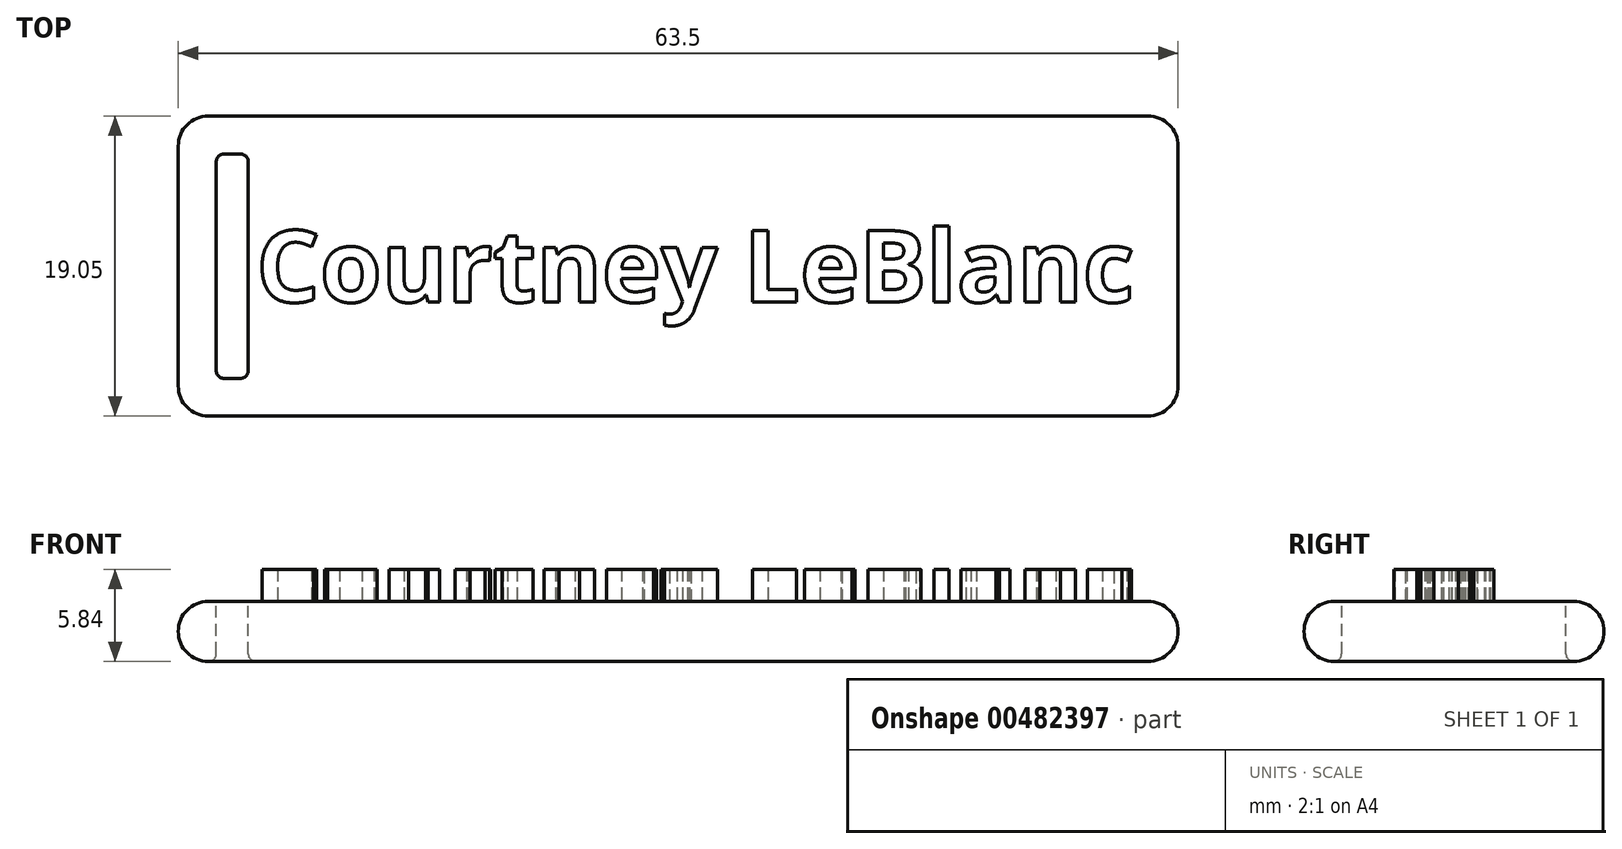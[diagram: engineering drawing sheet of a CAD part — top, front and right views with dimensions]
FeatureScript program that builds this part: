
annotation { "Feature Type Name" : "Feature", "Feature Type Description" : "" }
export const myFeature = defineFeature(function(context is Context, id is Id, definition is map)
    precondition{}
    {
        {
            var Q0;
            Q0=qCreatedBy(makeId("Top.planeOp"),FACE);
            var sketch = newSketch(context, id + "F0", { "sketchPlane" : qUnion([Q0])});
            skLineSegment(sketch, "E0.bottom", {"start": v(0, 0) * mm, "end": v(63.5, 0) * mm});
            skLineSegment(sketch, "E0.top", {"start": v(0, 19.05) * mm, "end": v(63.5, 19.05) * mm});
            skLineSegment(sketch, "E0.left", {"start": v(0, 0) * mm, "end": v(0, 19.05) * mm});
            skLineSegment(sketch, "E0.right", {"start": v(63.5, 0) * mm, "end": v(63.5, 19.05) * mm});
            skSolve(sketch);
        }
        {
            var Q0;
            Q0=makeQuery(id+"F0.imprint","IMPRINT",FACE,{"disambiguationData":[TD([[makeQuery(id+"F0.imprint","IMPRINT",EDGE,{"derivedFrom":sQuery(id+"F0.wireOp",EDGE,"E0.bottom")}),1.0]])]});
            extrude(context, id + "F1", {"entities" : qUnion([Q0]), "depth" : 3.8 * mm});
        }
        {
            var Q0;
            Q0=makeQuery(id+"F1.opExtrude","CAP_FACE",FACE,{"disambiguationData":[OSD([sQuery(id+"F0.wireOp",EDGE,"E0.bottom"),sQuery(id+"F0.wireOp",EDGE,"E0.top"),sQuery(id+"F0.wireOp",EDGE,"E0.left"),sQuery(id+"F0.wireOp",EDGE,"E0.right")])],"isStart":false});
            var sketch = newSketch(context, id + "F2", { "sketchPlane" : qUnion([Q0])});
            skText(sketch, "E1", { "text": "Courtney LeBlanc", "fontName": "OpenSans-Bold.ttf"});
            const initialGuessF2  = {"E1": [0.00495, 0.00724, 1, 0, 0.00457]};
            skSetInitialGuess(sketch, initialGuessF2);
            skSolve(sketch);
        }
        {
            var Q0;
            Q0 = qSketchRegion(id + "F2", true);
            extrude(context, id + "F3", {"entities" : qUnion([Q0]), "operationType" : NewBodyOperationType.ADD, "depth" : 2.03 * mm});
        }
        {
            var Q0;
            Q0=makeQuery(id+"F1.opExtrude","SWEPT_EDGE",EDGE,{"disambiguationData":[OSD([sQuery(id+"F0.wireOp",EDGE,"E0.top"),sQuery(id+"F0.wireOp",EDGE,"E0.right")])]});
            var Q1;
            Q1=makeQuery(id+"F1.opExtrude","CAP_EDGE",EDGE,{"disambiguationData":[OSD([sQuery(id+"F0.wireOp",EDGE,"E0.right")])],"isStart":false});
            var Q2;
            Q2=makeQuery(id+"F1.opExtrude","CAP_EDGE",EDGE,{"disambiguationData":[OSD([sQuery(id+"F0.wireOp",EDGE,"E0.top")])],"isStart":false});
            var Q3;
            Q3=makeQuery(id+"F1.opExtrude","CAP_EDGE",EDGE,{"disambiguationData":[OSD([sQuery(id+"F0.wireOp",EDGE,"E0.top")])],"isStart":true});
            var Q4;
            Q4=makeQuery(id+"F1.opExtrude","CAP_EDGE",EDGE,{"disambiguationData":[OSD([sQuery(id+"F0.wireOp",EDGE,"E0.right")])],"isStart":true});
            var Q5;
            Q5=makeQuery(id+"F1.opExtrude","SWEPT_EDGE",EDGE,{"disambiguationData":[OSD([sQuery(id+"F0.wireOp",EDGE,"E0.bottom"),sQuery(id+"F0.wireOp",EDGE,"E0.right")])]});
            var Q6;
            Q6=makeQuery(id+"F1.opExtrude","CAP_EDGE",EDGE,{"disambiguationData":[OSD([sQuery(id+"F0.wireOp",EDGE,"E0.bottom")])],"isStart":false});
            var Q7;
            Q7=makeQuery(id+"F1.opExtrude","CAP_EDGE",EDGE,{"disambiguationData":[OSD([sQuery(id+"F0.wireOp",EDGE,"E0.bottom")])],"isStart":true});
            var Q8;
            Q8=makeQuery(id+"F1.opExtrude","SWEPT_EDGE",EDGE,{"disambiguationData":[OSD([sQuery(id+"F0.wireOp",EDGE,"E0.bottom"),sQuery(id+"F0.wireOp",EDGE,"E0.left")])]});
            var Q9;
            Q9=makeQuery(id+"F1.opExtrude","CAP_EDGE",EDGE,{"disambiguationData":[OSD([sQuery(id+"F0.wireOp",EDGE,"E0.left")])],"isStart":false});
            var Q10;
            Q10=makeQuery(id+"F1.opExtrude","CAP_EDGE",EDGE,{"disambiguationData":[OSD([sQuery(id+"F0.wireOp",EDGE,"E0.left")])],"isStart":true});
            var Q11;
            Q11=makeQuery(id+"F1.opExtrude","SWEPT_EDGE",EDGE,{"disambiguationData":[OSD([sQuery(id+"F0.wireOp",EDGE,"E0.top"),sQuery(id+"F0.wireOp",EDGE,"E0.left")])]});
            fillet(context, id + "F4", {"entities" : qUnion([Q0, Q1, Q2, Q3, Q4, Q5, Q6, Q7, Q8, Q9, Q10, Q11]), "radius" : 1.9 * mm, "tangentPropagation" : true, "allowEdgeOverflow" : false});
        }
        {
            var Q0;
            {var subQ0=sQuery(id+"F0.wireOp",EDGE,"E0.bottom");var subQ1=sQuery(id+"F0.wireOp",EDGE,"E0.right");var subQ2=sQuery(id+"F0.wireOp",EDGE,"E0.top");var subQ3=sQuery(id+"F0.wireOp",EDGE,"E0.left");Q0=makeQuery(id+"F3.boolean.opBoolean","SPLIT",FACE,{"disambiguationData":[TD([makeQuery(id+"F1.opExtrude","SWEPT_FACE",FACE,{"disambiguationData":[OSD([subQ0])]})])],"derivedFrom":makeQuery(id+"F1.opExtrude","CAP_FACE",FACE,{"disambiguationData":[OSD([subQ0,subQ2,subQ3,subQ1])],"isStart":false})});}
            var sketch = newSketch(context, id + "F5", { "sketchPlane" : qUnion([Q0])});
            skLineSegment(sketch, "E2", {"start": v(1.9, 9.53) * mm, "end": v(2.41, 9.53) * mm});
            skLineSegment(sketch, "E3", {"start": v(2.41, 9.53) * mm, "end": v(2.41, 16.64) * mm});
            skLineSegment(sketch, "E4.bottom", {"start": v(2.41, 16.64) * mm, "end": v(4.45, 16.64) * mm});
            skLineSegment(sketch, "E4.top", {"start": v(2.41, 2.39) * mm, "end": v(4.45, 2.39) * mm});
            skLineSegment(sketch, "E4.left", {"start": v(2.41, 16.64) * mm, "end": v(2.41, 2.39) * mm});
            skLineSegment(sketch, "E4.right", {"start": v(4.45, 16.64) * mm, "end": v(4.45, 2.39) * mm});
            skSolve(sketch);
        }
        {
            var Q0;
            {var subQ3=sQuery(id+"F5.wireOp",EDGE,"E4.bottom");Q0=makeQuery(id+"F5.imprint","IMPRINT",FACE,{"disambiguationData":[TD([[makeQuery(id+"F5.imprint","IMPRINT",EDGE,{"derivedFrom":subQ3}),-1.0]])]});}
            extrude(context, id + "F6", {"entities" : qUnion([Q0]), "operationType" : NewBodyOperationType.REMOVE, "oppositeDirection" : true, "depth" : 25.4 * mm});
        }
        {
            var Q0;
            Q0=makeQuery(id+"F6.boolean.opBoolean","COPY",EDGE,{"derivedFrom":makeQuery(id+"F6.opExtrude","CAP_EDGE",EDGE,{"disambiguationData":[OSD([sQuery(id+"F5.wireOp",EDGE,"E4.left")])],"isStart":true})});
            var Q1;
            Q1=makeQuery(id+"F6.boolean.opBoolean","COPY",EDGE,{"derivedFrom":makeQuery(id+"F6.opExtrude","CAP_EDGE",EDGE,{"disambiguationData":[OSD([sQuery(id+"F5.wireOp",EDGE,"E4.bottom")])],"isStart":true})});
            var Q2;
            Q2=makeQuery(id+"F6.boolean.opBoolean","COPY",EDGE,{"derivedFrom":makeQuery(id+"F6.opExtrude","CAP_EDGE",EDGE,{"disambiguationData":[OSD([sQuery(id+"F5.wireOp",EDGE,"E4.right")])],"isStart":true})});
            var Q3;
            Q3=makeQuery(id+"F6.boolean.opBoolean","COPY",EDGE,{"derivedFrom":makeQuery(id+"F6.opExtrude","CAP_EDGE",EDGE,{"disambiguationData":[OSD([sQuery(id+"F5.wireOp",EDGE,"E4.top")])],"isStart":true})});
            var Q4;
            Q4=makeQuery(id+"F6.boolean.opBoolean","INTERSECT",EDGE,{"derivedFrom":[makeQuery(id+"F1.opExtrude","CAP_FACE",FACE,{"disambiguationData":[OSD([sQuery(id+"F0.wireOp",EDGE,"E0.bottom"),sQuery(id+"F0.wireOp",EDGE,"E0.top"),sQuery(id+"F0.wireOp",EDGE,"E0.left"),sQuery(id+"F0.wireOp",EDGE,"E0.right")])],"isStart":true}),makeQuery(id+"F6.opExtrude","SWEPT_FACE",FACE,{"disambiguationData":[OSD([sQuery(id+"F5.wireOp",EDGE,"E4.top")])]})]});
            var Q5;
            Q5=makeQuery(id+"F6.boolean.opBoolean","INTERSECT",EDGE,{"derivedFrom":[makeQuery(id+"F1.opExtrude","CAP_FACE",FACE,{"disambiguationData":[OSD([sQuery(id+"F0.wireOp",EDGE,"E0.bottom"),sQuery(id+"F0.wireOp",EDGE,"E0.top"),sQuery(id+"F0.wireOp",EDGE,"E0.left"),sQuery(id+"F0.wireOp",EDGE,"E0.right")])],"isStart":true}),makeQuery(id+"F6.opExtrude","SWEPT_FACE",FACE,{"disambiguationData":[OSD([sQuery(id+"F5.wireOp",EDGE,"E4.left")])]})]});
            var Q6;
            Q6=makeQuery(id+"F6.boolean.opBoolean","INTERSECT",EDGE,{"derivedFrom":[makeQuery(id+"F1.opExtrude","CAP_FACE",FACE,{"disambiguationData":[OSD([sQuery(id+"F0.wireOp",EDGE,"E0.bottom"),sQuery(id+"F0.wireOp",EDGE,"E0.top"),sQuery(id+"F0.wireOp",EDGE,"E0.left"),sQuery(id+"F0.wireOp",EDGE,"E0.right")])],"isStart":true}),makeQuery(id+"F6.opExtrude","SWEPT_FACE",FACE,{"disambiguationData":[OSD([sQuery(id+"F5.wireOp",EDGE,"E4.right")])]})]});
            var Q7;
            Q7=makeQuery(id+"F6.boolean.opBoolean","INTERSECT",EDGE,{"derivedFrom":[makeQuery(id+"F1.opExtrude","CAP_FACE",FACE,{"disambiguationData":[OSD([sQuery(id+"F0.wireOp",EDGE,"E0.bottom"),sQuery(id+"F0.wireOp",EDGE,"E0.top"),sQuery(id+"F0.wireOp",EDGE,"E0.left"),sQuery(id+"F0.wireOp",EDGE,"E0.right")])],"isStart":true}),makeQuery(id+"F6.opExtrude","SWEPT_FACE",FACE,{"disambiguationData":[OSD([sQuery(id+"F5.wireOp",EDGE,"E4.bottom")])]})]});
            var Q8;
            Q8=makeQuery(id+"F6.boolean.opBoolean","COPY",EDGE,{"derivedFrom":makeQuery(id+"F6.opExtrude","SWEPT_EDGE",EDGE,{"disambiguationData":[OSD([sQuery(id+"F5.wireOp",EDGE,"E4.bottom"),sQuery(id+"F5.wireOp",EDGE,"E4.right")])]})});
            var Q9;
            Q9=makeQuery(id+"F6.boolean.opBoolean","COPY",EDGE,{"derivedFrom":makeQuery(id+"F6.opExtrude","SWEPT_EDGE",EDGE,{"disambiguationData":[OSD([sQuery(id+"F5.wireOp",EDGE,"E4.bottom"),sQuery(id+"F5.wireOp",EDGE,"E4.left")])]})});
            var Q10;
            Q10=makeQuery(id+"F6.boolean.opBoolean","COPY",EDGE,{"derivedFrom":makeQuery(id+"F6.opExtrude","SWEPT_EDGE",EDGE,{"disambiguationData":[OSD([sQuery(id+"F5.wireOp",EDGE,"E4.top"),sQuery(id+"F5.wireOp",EDGE,"E4.left")])]})});
            var Q11;
            Q11=makeQuery(id+"F6.boolean.opBoolean","COPY",EDGE,{"derivedFrom":makeQuery(id+"F6.opExtrude","SWEPT_EDGE",EDGE,{"disambiguationData":[OSD([sQuery(id+"F5.wireOp",EDGE,"E4.top"),sQuery(id+"F5.wireOp",EDGE,"E4.right")])]})});
            fillet(context, id + "F7", {"entities" : qUnion([Q0, Q1, Q2, Q3, Q4, Q5, Q6, Q7, Q8, Q9, Q10, Q11]), "radius" : 0.48 * mm, "tangentPropagation" : true, "allowEdgeOverflow" : false});
        }
    });
